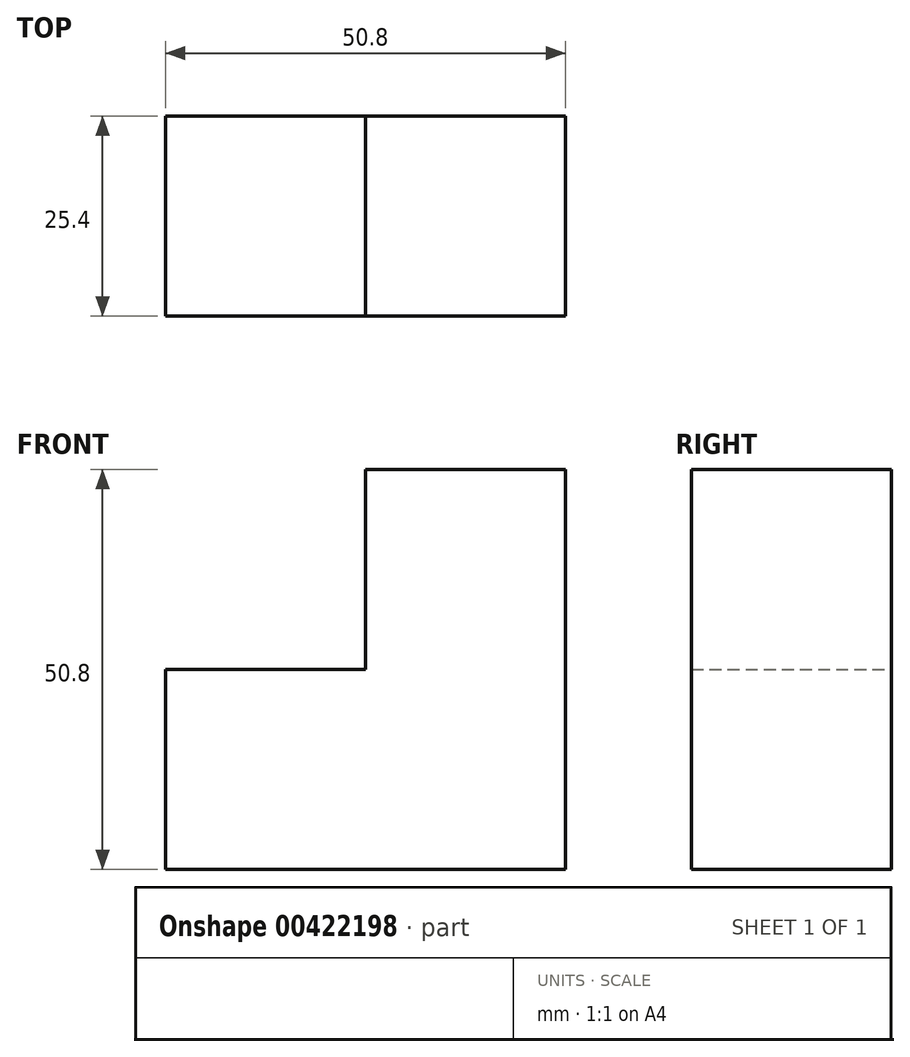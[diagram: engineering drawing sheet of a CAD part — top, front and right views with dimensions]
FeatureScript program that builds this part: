
annotation { "Feature Type Name" : "Feature", "Feature Type Description" : "" }
export const myFeature = defineFeature(function(context is Context, id is Id, definition is map)
    precondition{}
    {
        {
            var Q0;
            Q0=qCreatedBy(makeId("Front.planeOp"),FACE);
            var sketch = newSketch(context, id + "F0", { "sketchPlane" : qUnion([Q0])});
            skLineSegment(sketch, "E0", {"start": v(0, 0) * mm, "end": v(-50.8, 0) * mm});
            skLineSegment(sketch, "E1", {"start": v(-50.8, 0) * mm, "end": v(-50.8, 25.4) * mm});
            skLineSegment(sketch, "E2", {"start": v(-50.8, 25.4) * mm, "end": v(-25.4, 25.4) * mm});
            skLineSegment(sketch, "E3", {"start": v(-25.4, 25.4) * mm, "end": v(-25.4, 50.8) * mm});
            skLineSegment(sketch, "E4", {"start": v(-25.4, 50.8) * mm, "end": v(0, 50.8) * mm});
            skLineSegment(sketch, "E5", {"start": v(0, 0) * mm, "end": v(0, 50.8) * mm});
            skSolve(sketch);
        }
        {
            var Q0;
            Q0=makeQuery(id+"F0.imprint","IMPRINT",FACE,{"disambiguationData":[TD([[makeQuery(id+"F0.imprint","IMPRINT",EDGE,{"derivedFrom":sQuery(id+"F0.wireOp",EDGE,"E0")}),-1.0]])]});
            extrude(context, id + "F1", {"entities" : qUnion([Q0]), "depth" : 25.4 * mm});
        }
    });
